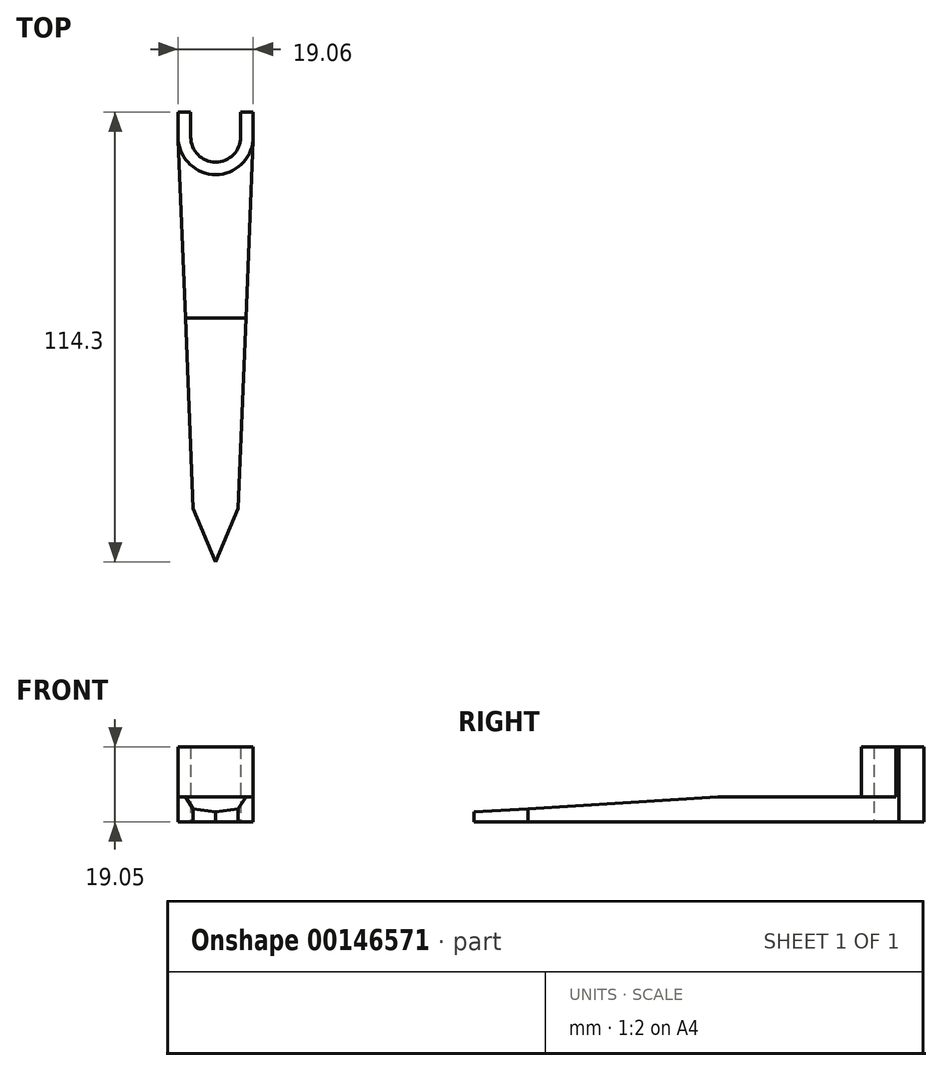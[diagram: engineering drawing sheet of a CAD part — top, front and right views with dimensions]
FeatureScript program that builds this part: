
annotation { "Feature Type Name" : "Feature", "Feature Type Description" : "" }
export const myFeature = defineFeature(function(context is Context, id is Id, definition is map)
    precondition{}
    {
        {
            var Q0;
            Q0=qCreatedBy(makeId("Top.planeOp"),FACE);
            var sketch = newSketch(context, id + "F0", { "sketchPlane" : qUnion([Q0])});
            skLineSegment(sketch, "E0", {"start": v(-5.72, 0) * mm, "end": v(0, -13.63) * mm});
            skLineSegment(sketch, "E1", {"start": v(0, -13.63) * mm, "end": v(0, 94.32) * mm, "construction": true});
            skLineSegment(sketch, "E2", {"start": v(-5.71, 0) * mm, "end": v(-9.52, 94.32) * mm});
            skLineSegment(sketch, "E3", {"start": v(-9.53, 94.32) * mm, "end": v(-6.35, 94.32) * mm});
            skArc(sketch, "E4", {"start": v(-6.35, 94.32) * mm, "mid": v(0, 87.97) * mm, "end": v(6.35, 94.32) * mm});
            skArc(sketch, "E5", {"start": v(-9.53, 94.32) * mm, "mid": v(0, 84.8) * mm, "end": v(9.53, 94.32) * mm});
            skLineSegment(sketch, "E6.MirrorCS", {"start": v(5.71, 0) * mm, "end": v(9.52, 94.32) * mm});
            skLineSegment(sketch, "E7.MirrorCS", {"start": v(9.53, 94.32) * mm, "end": v(6.35, 94.32) * mm});
            skLineSegment(sketch, "E8.MirrorCS", {"start": v(5.72, 0) * mm, "end": v(0, -13.63) * mm});
            skSolve(sketch);
        }
        {
            var Q0;
            {var subQ5=sQuery(id+"F0.wireOp",EDGE,"E0");Q0=makeQuery(id+"F0.imprint","IMPRINT",FACE,{"disambiguationData":[TD([[makeQuery(id+"F0.imprint","IMPRINT",EDGE,{"derivedFrom":subQ5}),1.0]])]});}
            extrude(context, id + "F1", {"entities" : qUnion([Q0]), "depth" : 6.35 * mm});
        }
        {
            var Q0;
            {var subQ5=sQuery(id+"F0.wireOp",EDGE,"E3");Q0=makeQuery(id+"F0.imprint","IMPRINT",FACE,{"disambiguationData":[TD([[makeQuery(id+"F0.imprint","IMPRINT",EDGE,{"derivedFrom":subQ5}),-1.0]])]});}
            extrude(context, id + "F2", {"entities" : qUnion([Q0]), "operationType" : NewBodyOperationType.ADD, "depth" : 19.05 * mm});
        }
        {
            var Q0;
            Q0=makeQuery(id+"F2.opExtrude","SWEPT_FACE",FACE,{"disambiguationData":[OSD([sQuery(id+"F0.wireOp",EDGE,"E3")])]});
            var Q1;
            Q1=makeQuery(id+"F2.opExtrude","SWEPT_FACE",FACE,{"disambiguationData":[OSD([sQuery(id+"F0.wireOp",EDGE,"E7.MirrorCS")])]});
            extrude(context, id + "F3", {"entities" : qUnion([Q0, Q1]), "operationType" : NewBodyOperationType.ADD, "depth" : 6.35 * mm});
        }
        {
            var Q0;
            Q0=qCreatedBy(makeId("Right.planeOp"),FACE);
            var sketch = newSketch(context, id + "F4", { "sketchPlane" : qUnion([Q0])});
            skLineSegment(sketch, "E9", {"start": v(-14.1, 2.5) * mm, "end": v(49.87, 6.45) * mm});
            skLineSegment(sketch, "E10", {"start": v(49.87, 6.45) * mm, "end": v(49.87, 26.77) * mm});
            skLineSegment(sketch, "E11", {"start": v(49.87, 26.77) * mm, "end": v(-30.66, 9.08) * mm});
            skLineSegment(sketch, "E12", {"start": v(-30.66, 9.08) * mm, "end": v(-14.1, 2.5) * mm});
            skSolve(sketch);
        }
        {
            var Q0;
            Q0 = qSketchRegion(id + "F4", true);
            extrude(context, id + "F5", {"entities" : qUnion([Q0]), "operationType" : NewBodyOperationType.REMOVE, "oppositeDirection" : true, "depth" : 25.4 * mm, "hasSecondDirection" : true, "secondDirectionOppositeDirection" : false, "secondDirectionDepth" : 25.4 * mm});
        }
    });
